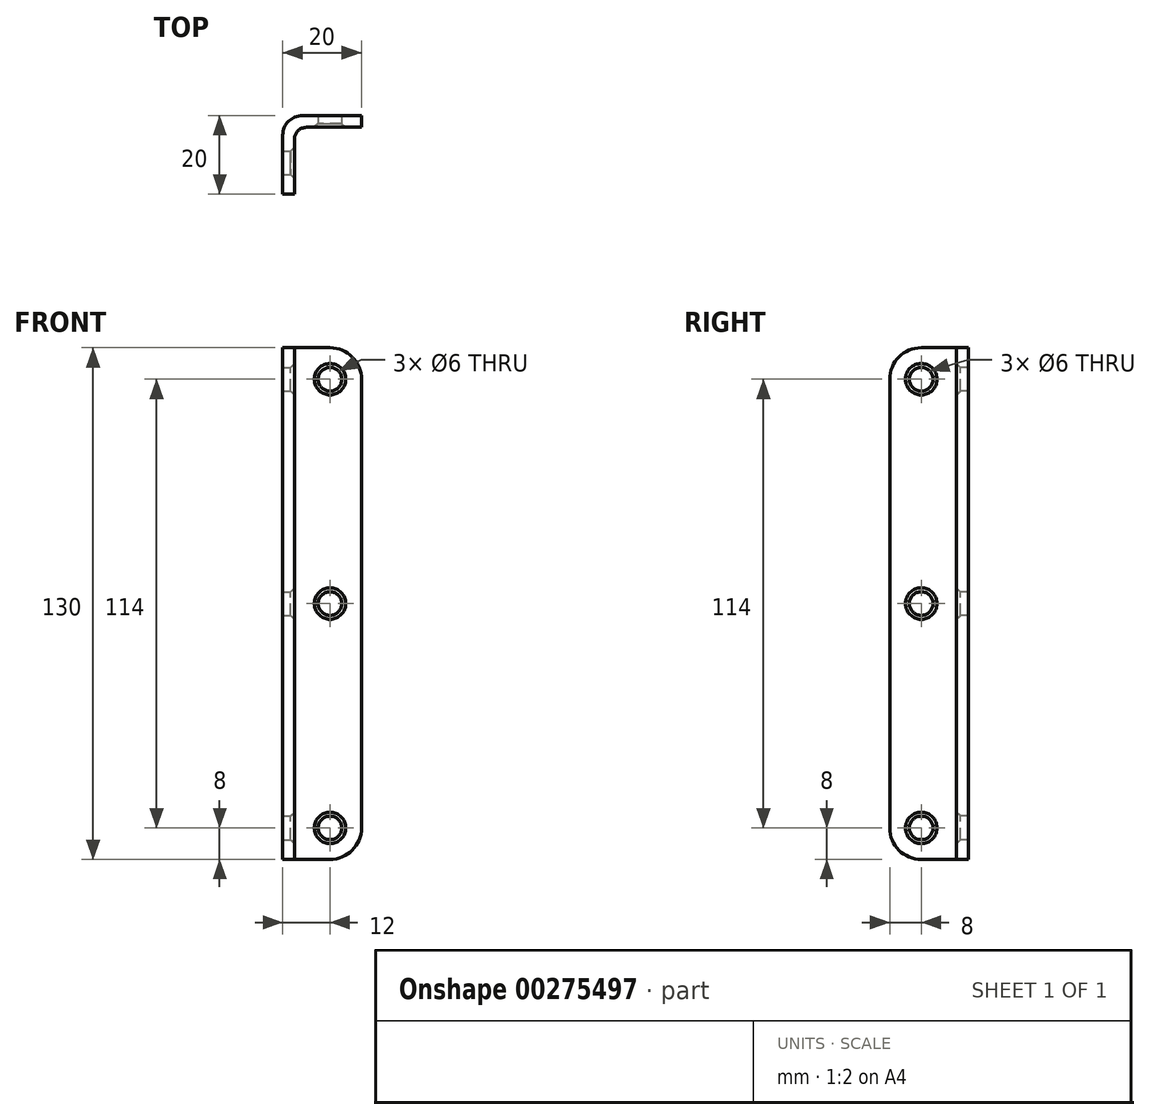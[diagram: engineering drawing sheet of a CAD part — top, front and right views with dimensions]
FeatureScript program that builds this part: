
annotation { "Feature Type Name" : "Feature", "Feature Type Description" : "" }
export const myFeature = defineFeature(function(context is Context, id is Id, definition is map)
    precondition{}
    {
        {
            var Q0;
            Q0=qCreatedBy(makeId("Top.planeOp"),FACE);
            var sketch = newSketch(context, id + "F0", { "sketchPlane" : qUnion([Q0])});
            skLineSegment(sketch, "E0", {"start": v(20, 0) * mm, "end": v(5, 0) * mm});
            skLineSegment(sketch, "E1", {"start": v(0, -5) * mm, "end": v(0, -20) * mm});
            skLineSegment(sketch, "E2", {"start": v(0, -20) * mm, "end": v(3, -20) * mm});
            skLineSegment(sketch, "E3", {"start": v(3, -20) * mm, "end": v(3, -6) * mm});
            skLineSegment(sketch, "E4", {"start": v(6, -3) * mm, "end": v(20, -3) * mm});
            skLineSegment(sketch, "E5", {"start": v(20, -3) * mm, "end": v(20, 0) * mm});
            skPoint(sketch, "E6.visualSharp", {"position": v(3, -3) * mm});
            skArc(sketch, "E6.filletArc", {"start": v(6, -3) * mm, "mid": v(3.88, -3.88) * mm, "end": v(3, -6) * mm});
            skPoint(sketch, "E7.visualSharp", {"position": v(0, 0) * mm});
            skArc(sketch, "E7.filletArc", {"start": v(5, 0) * mm, "mid": v(1.46, -1.46) * mm, "end": v(0, -5) * mm});
            skSolve(sketch);
        }
        {
            var Q0;
            Q0=makeQuery(id+"F0.imprint","IMPRINT",FACE,{"disambiguationData":[TD([[makeQuery(id+"F0.imprint","IMPRINT",EDGE,{"derivedFrom":sQuery(id+"F0.wireOp",EDGE,"E0")}),1.0]])]});
            extrude(context, id + "F1", {"entities" : qUnion([Q0]), "depth" : 130 * mm});
        }
        {
            var Q0;
            Q0=makeQuery(id+"F1.opExtrude","CAP_EDGE",EDGE,{"disambiguationData":[OSD([sQuery(id+"F0.wireOp",EDGE,"E5")])],"isStart":false});
            var Q1;
            Q1=makeQuery(id+"F1.opExtrude","CAP_EDGE",EDGE,{"disambiguationData":[OSD([sQuery(id+"F0.wireOp",EDGE,"E5")])],"isStart":true});
            var Q2;
            Q2=makeQuery(id+"F1.opExtrude","CAP_EDGE",EDGE,{"disambiguationData":[OSD([sQuery(id+"F0.wireOp",EDGE,"E2")])],"isStart":true});
            var Q3;
            Q3=makeQuery(id+"F1.opExtrude","CAP_EDGE",EDGE,{"disambiguationData":[OSD([sQuery(id+"F0.wireOp",EDGE,"E2")])],"isStart":false});
            fillet(context, id + "F2", {"entities" : qUnion([Q0, Q1, Q2, Q3]), "radius" : 8 * mm, "tangentPropagation" : true, "allowEdgeOverflow" : false});
        }
        {
            var Q0;
            Q0=makeQuery(id+"F1.opExtrude","SWEPT_FACE",FACE,{"disambiguationData":[OSD([sQuery(id+"F0.wireOp",EDGE,"E4")])]});
            var sketch = newSketch(context, id + "F3", { "sketchPlane" : qUnion([Q0])});
            skPoint(sketch, "E8", {"position": v(12, 122) * mm});
            skPoint(sketch, "E9", {"position": v(12, 8) * mm});
            skPoint(sketch, "E10", {"position": v(12, 65) * mm});
            skPoint(sketch, "E10.positionSnap0", {"position": v(20, 65) * mm});
            skSolve(sketch);
        }
        {
            var Q0;
            Q0=sQuery(id+"F3.wireOp",VERTEX,"E8");
            var Q1;
            Q1=sQuery(id+"F3.wireOp",VERTEX,"E10");
            var Q2;
            Q2=sQuery(id+"F3.wireOp",VERTEX,"E9");
            var Q3;
            Q3=makeQuery(id+"F1.opExtrude","SWEPT_BODY",BODY,{"disambiguationData":[OSD([sQuery(id+"F0.wireOp",EDGE,"E0"),sQuery(id+"F0.wireOp",EDGE,"E1"),sQuery(id+"F0.wireOp",EDGE,"E2"),sQuery(id+"F0.wireOp",EDGE,"E3"),sQuery(id+"F0.wireOp",EDGE,"E4"),sQuery(id+"F0.wireOp",EDGE,"E5"),sQuery(id+"F0.wireOp",EDGE,"E6.filletArc"),sQuery(id+"F0.wireOp",EDGE,"E7.filletArc")])]});
            hole(context, id + "F4", {"style" : HoleStyle.C_SINK, "endStyle" : HoleEndStyle.THROUGH, "standardTappedOrClearance" : lookupTablePath({ "standard" : "ISO", "size" : "6", "type" : "Drilled" }), "standardBlindInLast" : lookupTablePath({ "standard" : "ISO", "size" : "6", "type" : "Drilled" }), "holeDiameter" : 6 * mm, "cSinkDiameter" : 8 * mm, "cSinkAngle" : 90 * degree, "tappedDepth" : 12 * mm, "tapClearance" : 3, "locations" : qUnion([Q0, Q1, Q2]), "scope" : qUnion([Q3])});
        }
        {
            var Q0;
            Q0=makeQuery(id+"F1.opExtrude","SWEPT_FACE",FACE,{"disambiguationData":[OSD([sQuery(id+"F0.wireOp",EDGE,"E3")])]});
            var sketch = newSketch(context, id + "F5", { "sketchPlane" : qUnion([Q0])});
            skPoint(sketch, "E11", {"position": v(-12, 122) * mm});
            skPoint(sketch, "E12", {"position": v(-12, 8) * mm});
            skPoint(sketch, "E13", {"position": v(-12, 65) * mm});
            skPoint(sketch, "E13.positionSnap0", {"position": v(-20, 65) * mm});
            skSolve(sketch);
        }
        {
            var Q0;
            Q0=sQuery(id+"F5.wireOp",VERTEX,"E11");
            var Q1;
            Q1=sQuery(id+"F5.wireOp",VERTEX,"E13");
            var Q2;
            Q2=sQuery(id+"F5.wireOp",VERTEX,"E12");
            var Q3;
            Q3=makeQuery(id+"F1.opExtrude","SWEPT_BODY",BODY,{"disambiguationData":[OSD([sQuery(id+"F0.wireOp",EDGE,"E0"),sQuery(id+"F0.wireOp",EDGE,"E1"),sQuery(id+"F0.wireOp",EDGE,"E2"),sQuery(id+"F0.wireOp",EDGE,"E3"),sQuery(id+"F0.wireOp",EDGE,"E4"),sQuery(id+"F0.wireOp",EDGE,"E5"),sQuery(id+"F0.wireOp",EDGE,"E6.filletArc"),sQuery(id+"F0.wireOp",EDGE,"E7.filletArc")])]});
            hole(context, id + "F6", {"style" : HoleStyle.C_SINK, "endStyle" : HoleEndStyle.THROUGH, "standardTappedOrClearance" : lookupTablePath({ "standard" : "ISO", "size" : "6", "type" : "Drilled" }), "standardBlindInLast" : lookupTablePath({ "standard" : "ISO", "size" : "6", "type" : "Drilled" }), "holeDiameter" : 6 * mm, "cSinkDiameter" : 8 * mm, "cSinkAngle" : 90 * degree, "tappedDepth" : 12 * mm, "tapClearance" : 3, "locations" : qUnion([Q0, Q1, Q2]), "scope" : qUnion([Q3])});
        }
    });
